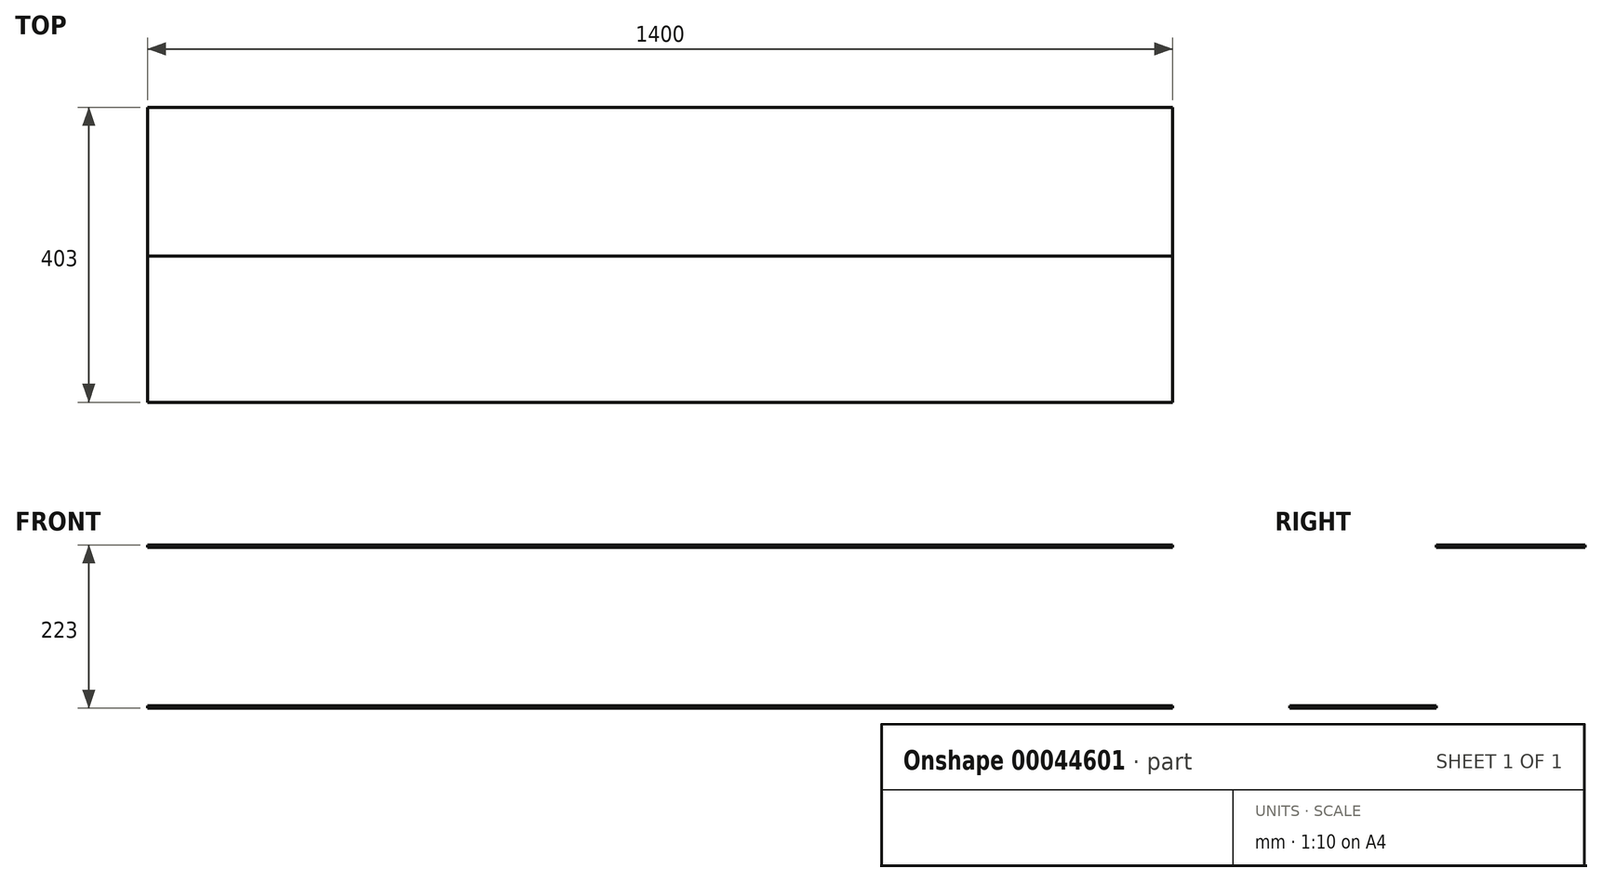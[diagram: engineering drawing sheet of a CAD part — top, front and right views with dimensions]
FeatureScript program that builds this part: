
annotation { "Feature Type Name" : "Feature", "Feature Type Description" : "" }
export const myFeature = defineFeature(function(context is Context, id is Id, definition is map)
    precondition{}
    {
        {
            var Q0;
            Q0=qCreatedBy(makeId("Right.planeOp"),FACE);
            var sketch = newSketch(context, id + "F0", { "sketchPlane" : qUnion([Q0])});
            skLineSegment(sketch, "E0.rect.bottom", {"start": v(-101.5, 1.5) * mm, "end": v(101.5, 1.5) * mm});
            skLineSegment(sketch, "E0.rect.top", {"start": v(-101.5, -1.5) * mm, "end": v(101.5, -1.5) * mm});
            skLineSegment(sketch, "E0.rect.left", {"start": v(-101.5, 1.5) * mm, "end": v(-101.5, -1.5) * mm});
            skLineSegment(sketch, "E0.rect.right", {"start": v(101.5, 1.5) * mm, "end": v(101.5, -1.5) * mm});
            skPoint(sketch, "E0.rect.middle", {"position": v(0, 0) * mm});
            skLineSegment(sketch, "E1.bottom", {"start": v(-101.5, -1.5) * mm, "end": v(-98.5, -1.5) * mm});
            skLineSegment(sketch, "E1.top", {"start": v(-101.5, -221.5) * mm, "end": v(-98.5, -221.5) * mm});
            skLineSegment(sketch, "E1.left", {"start": v(-101.5, -1.5) * mm, "end": v(-101.5, -221.5) * mm});
            skLineSegment(sketch, "E1.right", {"start": v(-98.5, -1.5) * mm, "end": v(-98.5, -221.5) * mm});
            skLineSegment(sketch, "E2.bottom", {"start": v(-101.5, -221.5) * mm, "end": v(-301.5, -221.5) * mm});
            skLineSegment(sketch, "E2.top", {"start": v(-101.5, -218.5) * mm, "end": v(-301.5, -218.5) * mm});
            skLineSegment(sketch, "E2.left", {"start": v(-101.5, -221.5) * mm, "end": v(-101.5, -218.5) * mm});
            skLineSegment(sketch, "E2.right", {"start": v(-301.5, -221.5) * mm, "end": v(-301.5, -218.5) * mm});
            skLineSegment(sketch, "E3.bottom", {"start": v(-301.5, -221.5) * mm, "end": v(-298.5, -221.5) * mm});
            skLineSegment(sketch, "E3.top", {"start": v(-301.5, -441.5) * mm, "end": v(-298.5, -441.5) * mm});
            skLineSegment(sketch, "E3.left", {"start": v(-301.5, -221.5) * mm, "end": v(-301.5, -441.5) * mm});
            skLineSegment(sketch, "E3.right", {"start": v(-298.5, -221.5) * mm, "end": v(-298.5, -441.5) * mm});
            skSolve(sketch);
        }
        {
            var Q0;
            Q0=makeQuery(id+"F0.imprint","IMPRINT",FACE,{"disambiguationData":[TD([[makeQuery(id+"F0.imprint","IMPRINT",EDGE,{"derivedFrom":sQuery(id+"F0.wireOp",EDGE,"E0.rect.bottom")}),-1.0]])]});
            var Q1;
            Q1=makeQuery(id+"F0.imprint","IMPRINT",FACE,{"disambiguationData":[TD([[makeQuery(id+"F0.imprint","IMPRINT",EDGE,{"derivedFrom":sQuery(id+"F0.wireOp",EDGE,"E1.bottom")}),-1.0]])]});
            var Q2;
            Q2=makeQuery(id+"F0.imprint","IMPRINT",FACE,{"disambiguationData":[TD([[makeQuery(id+"F0.imprint","IMPRINT",EDGE,{"derivedFrom":sQuery(id+"F0.wireOp",EDGE,"E2.bottom")}),-1.0]])]});
            var Q3;
            Q3=makeQuery(id+"F0.imprint","IMPRINT",FACE,{"disambiguationData":[TD([[makeQuery(id+"F0.imprint","IMPRINT",EDGE,{"derivedFrom":sQuery(id+"F0.wireOp",EDGE,"E3.bottom")}),-1.0]])]});
            extrude(context, id + "F1", {"entities" : qUnion([Q0, Q1, Q2, Q3]), "depth" : 1400 * mm});
        }
    });
